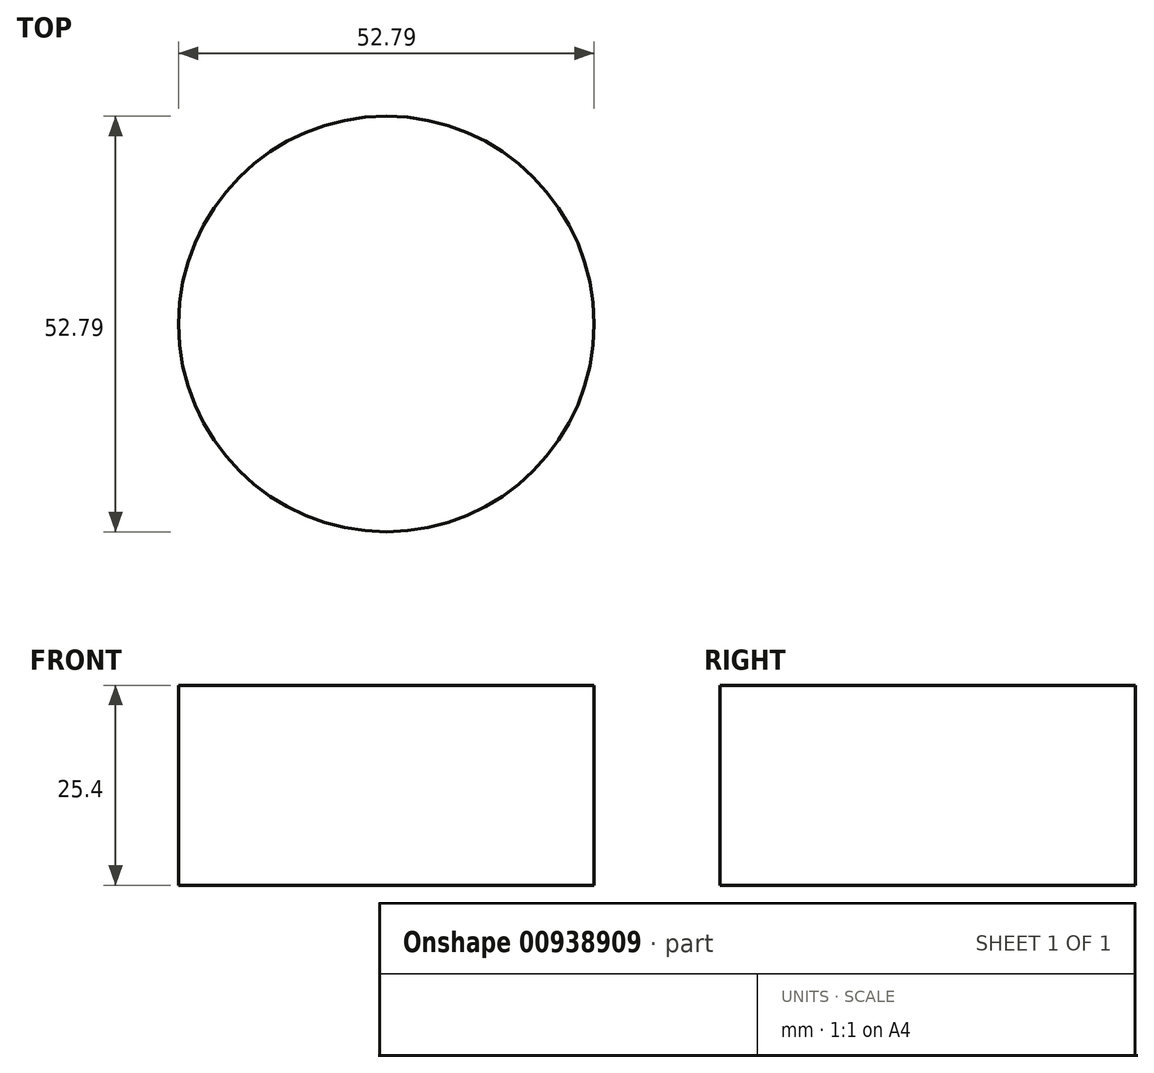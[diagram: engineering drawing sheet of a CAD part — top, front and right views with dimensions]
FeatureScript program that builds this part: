
annotation { "Feature Type Name" : "Feature", "Feature Type Description" : "" }
export const myFeature = defineFeature(function(context is Context, id is Id, definition is map)
    precondition{}
    {
        {
            var Q0;
            Q0=qCreatedBy(makeId("Top.planeOp"),FACE);
            var sketch = newSketch(context, id + "F0", { "sketchPlane" : qUnion([Q0])});
            skCircle(sketch, "E0", {"center": v(19.62, 17.02) * mm, "radius": 26.4 * mm});
            skSolve(sketch);
        }
        {
            var Q0;
            Q0=sQuery(id+"F0.wireOp",EDGE,"E0");
            extrude(context, id + "F1", {"bodyType" : ToolBodyType.SURFACE, "surfaceEntities" : qUnion([Q0]), "depth" : 25.4 * mm, "offsetDistance" : 25.4 * mm});
        }
    });
